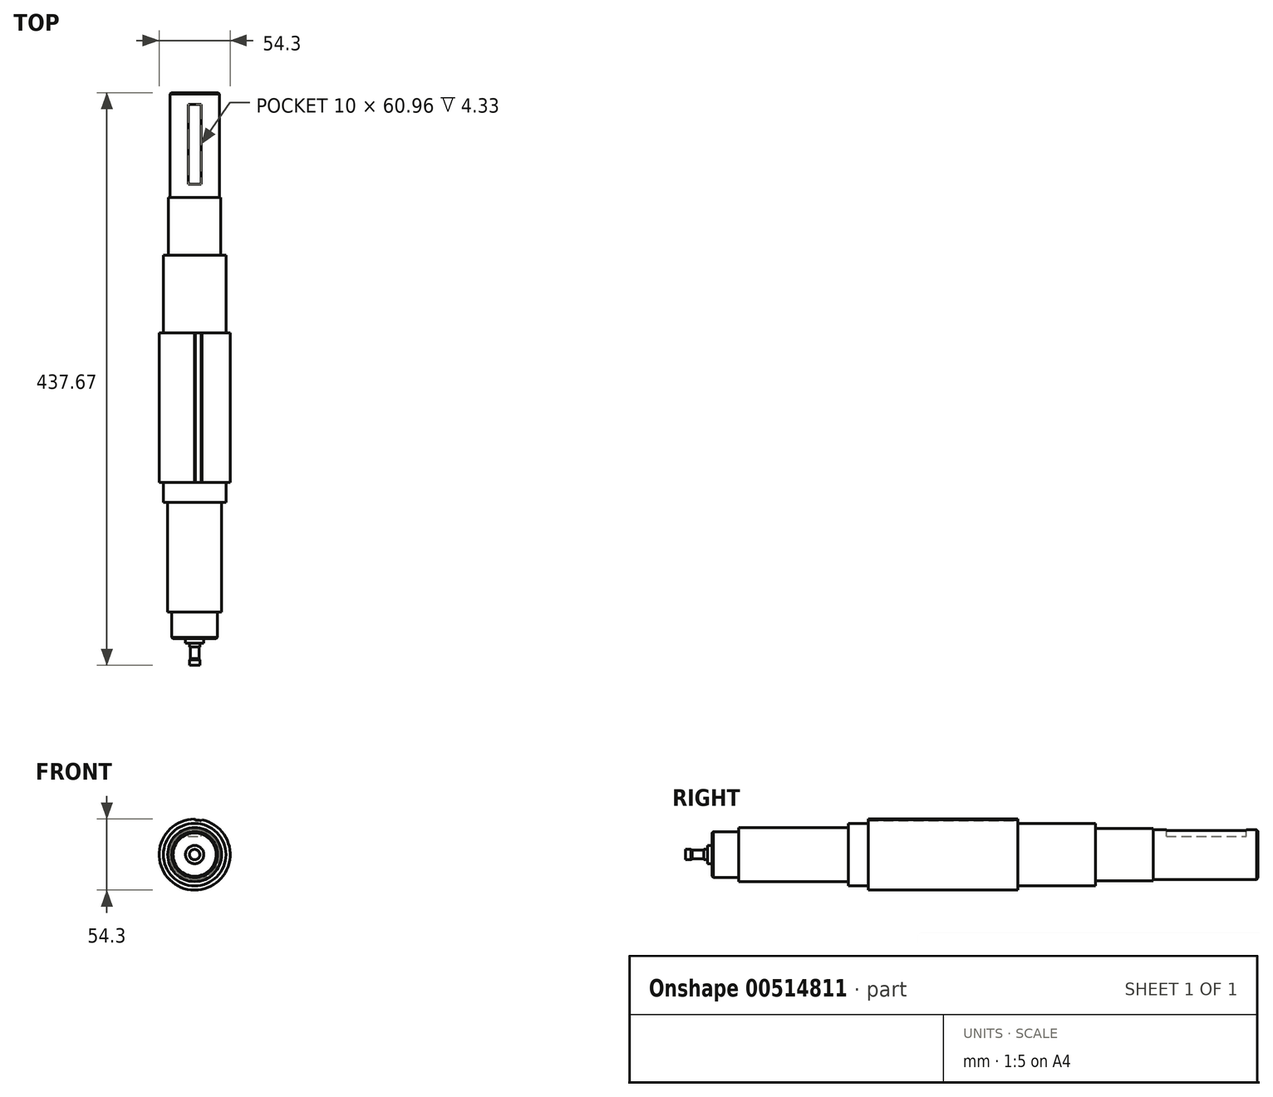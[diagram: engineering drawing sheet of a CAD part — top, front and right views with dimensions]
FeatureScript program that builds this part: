
annotation { "Feature Type Name" : "Feature", "Feature Type Description" : "" }
export const myFeature = defineFeature(function(context is Context, id is Id, definition is map)
    precondition{}
    {
        {
            var Q0;
            Q0=qCreatedBy(makeId("Right.planeOp"),FACE);
            var sketch = newSketch(context, id + "F0", { "sketchPlane" : qUnion([Q0])});
            skLineSegment(sketch, "E0", {"start": v(89.85, 0) * mm, "end": v(-136.66, 0) * mm, "construction": true});
            skLineSegment(sketch, "E1", {"start": v(0, 23.88) * mm, "end": v(59.26, 23.88) * mm});
            skLineSegment(sketch, "E2", {"start": v(59.26, 23.88) * mm, "end": v(59.26, 19.99) * mm});
            skLineSegment(sketch, "E3", {"start": v(59.26, 19.99) * mm, "end": v(103.43, 19.99) * mm});
            skLineSegment(sketch, "E4", {"start": v(103.43, 19.99) * mm, "end": v(103.43, 19) * mm});
            skLineSegment(sketch, "E5", {"start": v(103.43, 19) * mm, "end": v(183.44, 19) * mm});
            skLineSegment(sketch, "E6", {"start": v(183.44, 19) * mm, "end": v(183.44, 0) * mm});
            skLineSegment(sketch, "E7", {"start": v(0, 23.88) * mm, "end": v(0, 27.15) * mm});
            skLineSegment(sketch, "E8", {"start": v(0, 27.15) * mm, "end": v(-114.3, 27.15) * mm});
            skLineSegment(sketch, "E9", {"start": v(-114.3, 27.15) * mm, "end": v(-114.3, 23.88) * mm});
            skLineSegment(sketch, "E10", {"start": v(-114.3, 23.88) * mm, "end": v(-129.54, 23.88) * mm});
            skLineSegment(sketch, "E11", {"start": v(-129.54, 23.88) * mm, "end": v(-129.54, 20.64) * mm});
            skLineSegment(sketch, "E12", {"start": v(-129.54, 20.64) * mm, "end": v(-213.46, 20.64) * mm});
            skLineSegment(sketch, "E13", {"start": v(-213.46, 20.64) * mm, "end": v(-213.46, 17.5) * mm});
            skLineSegment(sketch, "E14", {"start": v(-213.46, 17.5) * mm, "end": v(-233.93, 17.5) * mm});
            skLineSegment(sketch, "E15", {"start": v(-233.93, 0) * mm, "end": v(183.44, 0) * mm});
            skLineSegment(sketch, "E16", {"start": v(-233.93, 17.5) * mm, "end": v(-233.93, 6.98) * mm});
            skLineSegment(sketch, "E17", {"start": v(-233.93, 6.98) * mm, "end": v(-237.24, 6.98) * mm});
            skLineSegment(sketch, "E18", {"start": v(-237.24, 6.98) * mm, "end": v(-237.24, 4) * mm});
            skLineSegment(sketch, "E19", {"start": v(-237.24, 4) * mm, "end": v(-240.23, 4) * mm});
            skLineSegment(sketch, "E20", {"start": v(-240.23, 4) * mm, "end": v(-240.23, 3.37) * mm});
            skLineSegment(sketch, "E21", {"start": v(-240.23, 3.37) * mm, "end": v(-249, 3.37) * mm});
            skLineSegment(sketch, "E22", {"start": v(-249, 3.37) * mm, "end": v(-250.09, 4) * mm});
            skLineSegment(sketch, "E23", {"start": v(-250.09, 4) * mm, "end": v(-254.23, 4) * mm});
            skLineSegment(sketch, "E24", {"start": v(-254.23, 4) * mm, "end": v(-254.23, 0) * mm});
            skLineSegment(sketch, "E25", {"start": v(-254.23, 0) * mm, "end": v(-233.93, 0) * mm});
            skSolve(sketch);
        }
        {
            var Q0;
            Q0=makeQuery(id+"F0.imprint","IMPRINT",FACE,{"disambiguationData":[TD([[makeQuery(id+"F0.imprint","IMPRINT",EDGE,{"derivedFrom":sQuery(id+"F0.wireOp",EDGE,"E1")}),-1.0]])]});
            var Q1;
            Q1=sQuery(id+"F0.wireOp",EDGE,"E15");
            revolve(context, id + "F1", {"entities" : qUnion([Q0]), "axis" : qUnion([Q1]), "revolveType" : RevolveType.FULL});
        }
        {
            var Q0;
            Q0=makeQuery(id+"F1.opRevolve","SWEPT_FACE",FACE,{"disambiguationData":[OSD([sQuery(id+"F0.wireOp",EDGE,"E7")])]});
            var sketch = newSketch(context, id + "F2", { "sketchPlane" : qUnion([Q0])});
            skLineSegment(sketch, "E26", {"start": v(0, 28.92) * mm, "end": v(0, 0) * mm, "construction": true});
            skLineSegment(sketch, "E27", {"start": v(0, 0) * mm, "end": v(-6.07, 28.55) * mm, "construction": true});
            skLineSegment(sketch, "E28", {"start": v(0, 0) * mm, "end": v(-2.96, 28.14) * mm, "construction": true});
            skLineSegment(sketch, "E29", {"start": v(0, 27.15) * mm, "end": v(-0.44, 26.39) * mm});
            skCircle(sketch, "E30", {"center": v(0, 0) * mm, "radius": 26.4 * mm, "construction": true});
            skLineSegment(sketch, "E31.MirrorCS", {"start": v(-5.65, 26.56) * mm, "end": v(-5.05, 25.9) * mm});
            skArc(sketch, "E32", {"start": v(-0.44, 26.39) * mm, "mid": v(-2.76, 26.25) * mm, "end": v(-5.05, 25.9) * mm});
            skSolve(sketch);
        }
        {
            var Q0;
            {var subQ0=sQuery(id+"F2.wireOp",EDGE,"E29");Q0=makeQuery(id+"F2.imprint","IMPRINT",FACE,{"disambiguationData":[TD([[makeQuery(id+"F2.imprint","IMPRINT",EDGE,{"derivedFrom":subQ0}),-1.0]])]});}
            extrude(context, id + "F3", {"entities" : qUnion([Q0]), "operationType" : NewBodyOperationType.REMOVE, "endBound" : BoundingType.THROUGH_ALL, "oppositeDirection" : true, "depth" : 25.4 * mm, "offsetDistance" : 25.4 * mm});
        }
        {
            var Q0;
            Q0=qCreatedBy(makeId("Top.planeOp"),FACE);
            cPlane(context, id + "F4", {"entities" : qUnion([Q0]), "cplaneType" : CPlaneType.OFFSET, "offset" : 19 * mm, "width" : 152.4 * mm, "height" : 152.4 * mm});
        }
        {
            var Q0;
            Q0=qCreatedBy(id+"F4.planeOp",FACE);
            var sketch = newSketch(context, id + "F5", { "sketchPlane" : qUnion([Q0])});
            skLineSegment(sketch, "E33", {"start": v(0, 182.27) * mm, "end": v(0, 95.54) * mm, "construction": true});
            skLineSegment(sketch, "E34", {"start": v(-5, 113.49) * mm, "end": v(-5, 174.45) * mm});
            skLineSegment(sketch, "E35", {"start": v(0, 174.45) * mm, "end": v(-5, 174.45) * mm});
            skLineSegment(sketch, "E36", {"start": v(0, 174.45) * mm, "end": v(5, 174.45) * mm});
            skLineSegment(sketch, "E37.MirrorCS", {"start": v(5, 113.49) * mm, "end": v(5, 174.45) * mm});
            skLineSegment(sketch, "E38", {"start": v(-5, 113.49) * mm, "end": v(5, 113.49) * mm});
            skSolve(sketch);
        }
        {
            var Q0;
            Q0=makeQuery(id+"F5.imprint","IMPRINT",FACE,{"disambiguationData":[TD([[makeQuery(id+"F5.imprint","IMPRINT",EDGE,{"derivedFrom":sQuery(id+"F5.wireOp",EDGE,"E34")}),-1.0]])]});
            extrude(context, id + "F6", {"entities" : qUnion([Q0]), "operationType" : NewBodyOperationType.REMOVE, "oppositeDirection" : true, "depth" : 5 * mm, "offsetDistance" : 25.4 * mm});
        }
        {
            var Q0;
            Q0=makeQuery(id+"F1.opRevolve","SWEPT_EDGE",EDGE,{"disambiguationData":[OSD([sQuery(id+"F0.wireOp",EDGE,"E5"),sQuery(id+"F0.wireOp",EDGE,"E6")])]});
            var Q1;
            Q1=makeQuery(id+"F1.opRevolve","SWEPT_EDGE",EDGE,{"disambiguationData":[OSD([sQuery(id+"F0.wireOp",EDGE,"E14"),sQuery(id+"F0.wireOp",EDGE,"E16")])]});
            chamfer(context, id + "F7", {"entities" : qUnion([Q0, Q1]), "width" : 1.02 * mm, "tangentPropagation" : true});
        }
    });
